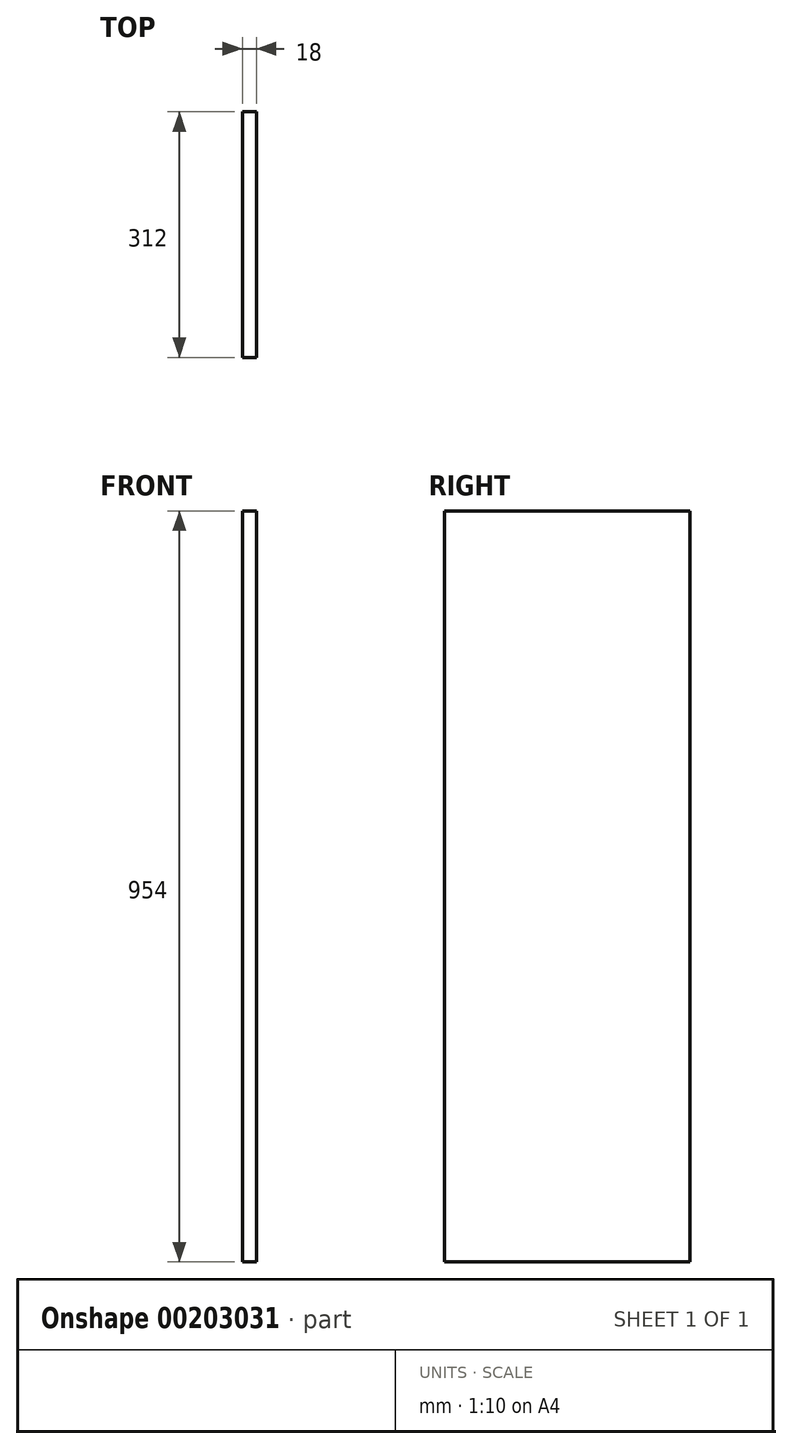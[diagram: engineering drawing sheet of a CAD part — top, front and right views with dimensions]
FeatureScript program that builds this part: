
annotation { "Feature Type Name" : "Feature", "Feature Type Description" : "" }
export const myFeature = defineFeature(function(context is Context, id is Id, definition is map)
    precondition{}
    {
        {
            var Q0;
            Q0=qCreatedBy(makeId("Right.planeOp"),FACE);
            var sketch = newSketch(context, id + "F0", { "sketchPlane" : qUnion([Q0])});
            skLineSegment(sketch, "E0.bottom", {"start": v(-156, -477) * mm, "end": v(156, -477) * mm});
            skLineSegment(sketch, "E0.top", {"start": v(-156, 477) * mm, "end": v(156, 477) * mm});
            skLineSegment(sketch, "E0.left", {"start": v(-156, -477) * mm, "end": v(-156, 477) * mm});
            skLineSegment(sketch, "E0.right", {"start": v(156, -477) * mm, "end": v(156, 477) * mm});
            skPoint(sketch, "E0.middle", {"position": v(0, 0) * mm});
            skSolve(sketch);
        }
        {
            var Q0;
            Q0=qSketchRegion(id+"F0",true);
            extrude(context, id + "F1", {"entities" : qUnion([Q0]), "depth" : 18 * mm});
        }
    });
